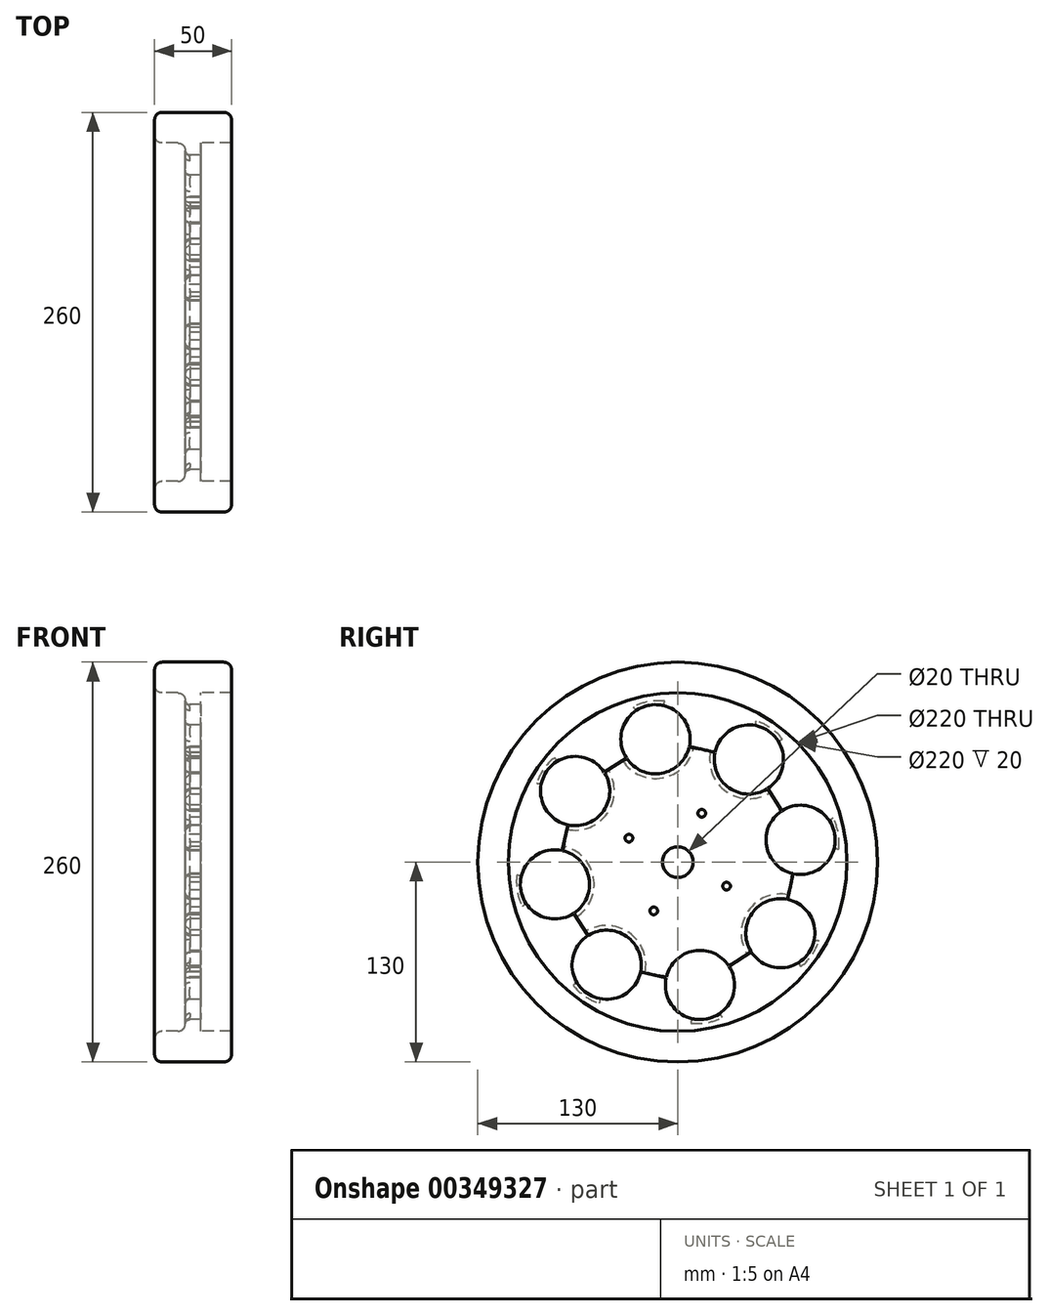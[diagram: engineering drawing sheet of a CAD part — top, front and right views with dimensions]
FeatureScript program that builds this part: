
annotation { "Feature Type Name" : "Feature", "Feature Type Description" : "" }
export const myFeature = defineFeature(function(context is Context, id is Id, definition is map)
    precondition{}
    {
        {
            var Q0;
            Q0=qCreatedBy(makeId("Right.planeOp"),FACE);
            var sketch = newSketch(context, id + "F0", { "sketchPlane" : qUnion([Q0])});
            skCircle(sketch, "E0", {"center": v(0, 0) * mm, "radius": 130 * mm});
            skCircle(sketch, "E1", {"center": v(0, 0) * mm, "radius": 110 * mm});
            skCircle(sketch, "E2", {"center": v(0, 0) * mm, "radius": 75 * mm});
            skCircle(sketch, "E3", {"center": v(0, 0) * mm, "radius": 10 * mm});
            skLineSegment(sketch, "E4.0", {"start": v(-31.73, 15.6) * mm, "end": v(15.6, 31.73) * mm});
            skLineSegment(sketch, "E4.1", {"start": v(15.6, 31.73) * mm, "end": v(31.73, -15.6) * mm});
            skLineSegment(sketch, "E4.2", {"start": v(31.73, -15.6) * mm, "end": v(-15.6, -31.73) * mm});
            skLineSegment(sketch, "E4.3", {"start": v(-15.6, -31.73) * mm, "end": v(-31.73, 15.6) * mm});
            skPoint(sketch, "E4.0.midPoint", {"position": v(-8.06, 23.66) * mm});
            skLineSegment(sketch, "E5.0", {"start": v(-66.72, 46.24) * mm, "end": v(-14.48, 79.88) * mm});
            skLineSegment(sketch, "E5.1", {"start": v(-14.48, 79.88) * mm, "end": v(46.24, 66.72) * mm});
            skLineSegment(sketch, "E5.2", {"start": v(46.24, 66.72) * mm, "end": v(79.88, 14.48) * mm});
            skLineSegment(sketch, "E5.3", {"start": v(79.88, 14.48) * mm, "end": v(66.72, -46.24) * mm});
            skLineSegment(sketch, "E5.4", {"start": v(66.72, -46.24) * mm, "end": v(14.48, -79.88) * mm});
            skLineSegment(sketch, "E5.5", {"start": v(14.48, -79.88) * mm, "end": v(-46.24, -66.72) * mm});
            skLineSegment(sketch, "E5.6", {"start": v(-46.24, -66.72) * mm, "end": v(-79.88, -14.48) * mm});
            skLineSegment(sketch, "E5.7", {"start": v(-79.88, -14.48) * mm, "end": v(-66.72, 46.24) * mm});
            skPoint(sketch, "E5.0.midPoint", {"position": v(-40.6, 63.06) * mm});
            skCircle(sketch, "E6", {"center": v(-31.73, 15.6) * mm, "radius": 2.5 * mm});
            skCircle(sketch, "E7", {"center": v(15.6, 31.73) * mm, "radius": 2.5 * mm});
            skCircle(sketch, "E8", {"center": v(31.73, -15.6) * mm, "radius": 2.5 * mm});
            skCircle(sketch, "E9", {"center": v(-15.6, -31.73) * mm, "radius": 2.5 * mm});
            skCircle(sketch, "E10", {"center": v(-46.24, -66.72) * mm, "radius": 22.5 * mm});
            skCircle(sketch, "E11", {"center": v(14.48, -79.88) * mm, "radius": 22.5 * mm});
            skCircle(sketch, "E12", {"center": v(66.72, -46.24) * mm, "radius": 22.5 * mm});
            skCircle(sketch, "E13", {"center": v(79.88, 14.48) * mm, "radius": 22.5 * mm});
            skCircle(sketch, "E14", {"center": v(46.24, 66.72) * mm, "radius": 22.5 * mm});
            skCircle(sketch, "E15", {"center": v(-14.48, 79.88) * mm, "radius": 22.5 * mm});
            skCircle(sketch, "E16", {"center": v(-66.72, 46.24) * mm, "radius": 22.5 * mm});
            skCircle(sketch, "E17", {"center": v(-79.88, -14.48) * mm, "radius": 22.5 * mm});
            skSolve(sketch);
        }
        {
            var Q0;
            Q0 = qSketchRegion(id + "F0", true);
            extrude(context, id + "F1", {"entities" : qUnion([Q0]), "endBound" : BoundingType.SYMMETRIC, "depth" : 50 * mm});
        }
        {
            var Q0;
            {var subQ0=sQuery(id+"F0.wireOp",EDGE,"E2");var subQ29=makeQuery(id+"F0.imprint","INTERSECT",VERTEX,{"derivedFrom":[subQ0,sQuery(id+"F0.wireOp",EDGE,"E5.2")]});Q0=makeQuery(id+"F0.imprint","IMPRINT",FACE,{"disambiguationData":[TD([[makeQuery(id+"F0.imprint","IMPRINT",EDGE,{"disambiguationData":[TD([[subQ29,1.0]])],"derivedFrom":subQ0}),1.0]])]});}
            var Q1;
            Q1=makeQuery(id+"F0.imprint","IMPRINT",FACE,{"disambiguationData":[TD([[makeQuery(id+"F0.imprint","IMPRINT",EDGE,{"derivedFrom":sQuery(id+"F0.wireOp",EDGE,"E1")}),1.0]])]});
            var Q2;
            Q2=makeQuery(id+"F0.imprint","IMPRINT",FACE,{"disambiguationData":[TD([[makeQuery(id+"F0.imprint","IMPRINT",EDGE,{"derivedFrom":sQuery(id+"F0.wireOp",EDGE,"E3")}),-1.0]])]});
            extrude(context, id + "F2", {"entities" : qUnion([Q0, Q1, Q2]), "operationType" : NewBodyOperationType.ADD, "endBound" : BoundingType.SYMMETRIC, "depth" : 10 * mm});
        }
        {
            var Q0;
            {var subQ0=sQuery(id+"F0.wireOp",EDGE,"E1");Q0=makeQuery(id+"F2.boolean.opBoolean","SPLIT",FACE,{"disambiguationData":[TD([makeQuery(id+"F1.opExtrude","CAP_FACE",FACE,{"disambiguationData":[OSD([sQuery(id+"F0.wireOp",EDGE,"E0"),subQ0])],"isStart":true})])],"derivedFrom":makeQuery(id+"F1.opExtrude","SWEPT_FACE",FACE,{"disambiguationData":[OSD([subQ0])]})});}
            fillet(context, id + "F3", {"entities" : qUnion([Q0]), "radius" : 5 * mm, "tangentPropagation" : true, "allowEdgeOverflow" : false});
        }
        {
            var Q0;
            Q0=makeQuery(id+"F1.opExtrude","CAP_EDGE",EDGE,{"disambiguationData":[OSD([sQuery(id+"F0.wireOp",EDGE,"E0")])],"isStart":true});
            var Q1;
            Q1=makeQuery(id+"F1.opExtrude","CAP_EDGE",EDGE,{"disambiguationData":[OSD([sQuery(id+"F0.wireOp",EDGE,"E0")])],"isStart":false});
            fillet(context, id + "F4", {"entities" : qUnion([Q0, Q1]), "radius" : 5 * mm, "tangentPropagation" : true, "allowEdgeOverflow" : false});
        }
        {
            var Q0;
            {var subQ0=sQuery(id+"F0.wireOp",EDGE,"E14");Q0=makeQuery(id+"F2.opExtrude","CAP_EDGE",EDGE,{"disambiguationData":[OSD([subQ0]),TDD([makeQuery(id+"F0.imprint","IMPRINT",EDGE,{"disambiguationData":[TD([[makeQuery(id+"F0.imprint","INTERSECT",VERTEX,{"derivedFrom":[sQuery(id+"F0.wireOp",EDGE,"E5.1"),subQ0]}),1.0]])],"derivedFrom":subQ0})])],"isStart":true});}
            var Q1;
            {var subQ0=sQuery(id+"F0.wireOp",EDGE,"E15");Q1=makeQuery(id+"F2.opExtrude","CAP_EDGE",EDGE,{"disambiguationData":[OSD([subQ0]),TDD([makeQuery(id+"F0.imprint","IMPRINT",EDGE,{"disambiguationData":[TD([[makeQuery(id+"F0.imprint","INTERSECT",VERTEX,{"derivedFrom":[sQuery(id+"F0.wireOp",EDGE,"E5.0"),subQ0]}),1.0]])],"derivedFrom":subQ0})])],"isStart":true});}
            var Q2;
            {var subQ0=sQuery(id+"F0.wireOp",EDGE,"E16");Q2=makeQuery(id+"F2.opExtrude","CAP_EDGE",EDGE,{"disambiguationData":[OSD([subQ0]),TDD([makeQuery(id+"F0.imprint","IMPRINT",EDGE,{"disambiguationData":[TD([[makeQuery(id+"F0.imprint","INTERSECT",VERTEX,{"derivedFrom":[sQuery(id+"F0.wireOp",EDGE,"E5.0"),subQ0]}),-1.0]])],"derivedFrom":subQ0})])],"isStart":true});}
            var Q3;
            {var subQ0=sQuery(id+"F0.wireOp",EDGE,"E13");Q3=makeQuery(id+"F2.opExtrude","CAP_EDGE",EDGE,{"disambiguationData":[OSD([subQ0]),TDD([makeQuery(id+"F0.imprint","IMPRINT",EDGE,{"disambiguationData":[TD([[makeQuery(id+"F0.imprint","INTERSECT",VERTEX,{"derivedFrom":[sQuery(id+"F0.wireOp",EDGE,"E5.2"),subQ0]}),1.0]])],"derivedFrom":subQ0})])],"isStart":true});}
            var Q4;
            {var subQ0=sQuery(id+"F0.wireOp",EDGE,"E12");Q4=makeQuery(id+"F2.opExtrude","CAP_EDGE",EDGE,{"disambiguationData":[OSD([subQ0]),TDD([makeQuery(id+"F0.imprint","IMPRINT",EDGE,{"disambiguationData":[TD([[makeQuery(id+"F0.imprint","INTERSECT",VERTEX,{"derivedFrom":[sQuery(id+"F0.wireOp",EDGE,"E5.3"),subQ0]}),1.0]])],"derivedFrom":subQ0})])],"isStart":true});}
            var Q5;
            {var subQ0=sQuery(id+"F0.wireOp",EDGE,"E11");Q5=makeQuery(id+"F2.opExtrude","CAP_EDGE",EDGE,{"disambiguationData":[OSD([subQ0]),TDD([makeQuery(id+"F0.imprint","IMPRINT",EDGE,{"disambiguationData":[TD([[makeQuery(id+"F0.imprint","INTERSECT",VERTEX,{"derivedFrom":[sQuery(id+"F0.wireOp",EDGE,"E5.4"),subQ0]}),1.0]])],"derivedFrom":subQ0})])],"isStart":true});}
            var Q6;
            {var subQ0=sQuery(id+"F0.wireOp",EDGE,"E17");Q6=makeQuery(id+"F2.opExtrude","CAP_EDGE",EDGE,{"disambiguationData":[OSD([subQ0]),TDD([makeQuery(id+"F0.imprint","IMPRINT",EDGE,{"disambiguationData":[TD([[makeQuery(id+"F0.imprint","INTERSECT",VERTEX,{"derivedFrom":[sQuery(id+"F0.wireOp",EDGE,"E5.6"),subQ0]}),1.0]])],"derivedFrom":subQ0})])],"isStart":true});}
            var Q7;
            {var subQ0=sQuery(id+"F0.wireOp",EDGE,"E10");Q7=makeQuery(id+"F2.opExtrude","CAP_EDGE",EDGE,{"disambiguationData":[OSD([subQ0]),TDD([makeQuery(id+"F0.imprint","IMPRINT",EDGE,{"disambiguationData":[TD([[makeQuery(id+"F0.imprint","INTERSECT",VERTEX,{"derivedFrom":[sQuery(id+"F0.wireOp",EDGE,"E5.5"),subQ0]}),1.0]])],"derivedFrom":subQ0})])],"isStart":true});}
            fillet(context, id + "F5", {"entities" : qUnion([Q0, Q1, Q2, Q3, Q4, Q5, Q6, Q7]), "radius" : 3 * mm, "tangentPropagation" : true, "allowEdgeOverflow" : false});
        }
        {
            var Q0;
            {var subQ0=sQuery(id+"F0.wireOp",EDGE,"E11");var subQ1=sQuery(id+"F0.wireOp",EDGE,"E2");Q0=makeQuery(id+"F2.opExtrude","CAP_EDGE",EDGE,{"disambiguationData":[OSD([subQ0]),TDD([makeQuery(id+"F0.imprint","IMPRINT",EDGE,{"disambiguationData":[TD([[makeQuery(id+"F0.imprint","INTERSECT",VERTEX,{"disambiguationData":[OD(0.0)],"derivedFrom":[subQ1,subQ0]}),1.0]])],"derivedFrom":subQ0})])],"isStart":true});}
            var Q1;
            {var subQ0=sQuery(id+"F0.wireOp",EDGE,"E10");var subQ1=sQuery(id+"F0.wireOp",EDGE,"E2");Q1=makeQuery(id+"F2.opExtrude","CAP_EDGE",EDGE,{"disambiguationData":[OSD([subQ0]),TDD([makeQuery(id+"F0.imprint","IMPRINT",EDGE,{"disambiguationData":[TD([[makeQuery(id+"F0.imprint","INTERSECT",VERTEX,{"disambiguationData":[OD(0.0)],"derivedFrom":[subQ1,subQ0]}),1.0]])],"derivedFrom":subQ0})])],"isStart":true});}
            var Q2;
            {var subQ0=sQuery(id+"F0.wireOp",EDGE,"E17");var subQ1=sQuery(id+"F0.wireOp",EDGE,"E2");Q2=makeQuery(id+"F2.opExtrude","CAP_EDGE",EDGE,{"disambiguationData":[OSD([subQ0]),TDD([makeQuery(id+"F0.imprint","IMPRINT",EDGE,{"disambiguationData":[TD([[makeQuery(id+"F0.imprint","INTERSECT",VERTEX,{"disambiguationData":[OD(0.0)],"derivedFrom":[subQ1,subQ0]}),1.0]])],"derivedFrom":subQ0})])],"isStart":true});}
            var Q3;
            {var subQ0=sQuery(id+"F0.wireOp",EDGE,"E16");var subQ1=sQuery(id+"F0.wireOp",EDGE,"E2");Q3=makeQuery(id+"F2.opExtrude","CAP_EDGE",EDGE,{"disambiguationData":[OSD([subQ0]),TDD([makeQuery(id+"F0.imprint","IMPRINT",EDGE,{"disambiguationData":[TD([[makeQuery(id+"F0.imprint","INTERSECT",VERTEX,{"disambiguationData":[OD(0.0)],"derivedFrom":[subQ1,subQ0]}),1.0]])],"derivedFrom":subQ0})])],"isStart":true});}
            var Q4;
            {var subQ0=sQuery(id+"F0.wireOp",EDGE,"E12");var subQ1=sQuery(id+"F0.wireOp",EDGE,"E2");Q4=makeQuery(id+"F2.opExtrude","CAP_EDGE",EDGE,{"disambiguationData":[OSD([subQ0]),TDD([makeQuery(id+"F0.imprint","IMPRINT",EDGE,{"disambiguationData":[TD([[makeQuery(id+"F0.imprint","INTERSECT",VERTEX,{"disambiguationData":[OD(0.0)],"derivedFrom":[subQ1,subQ0]}),1.0]])],"derivedFrom":subQ0})])],"isStart":true});}
            var Q5;
            {var subQ0=sQuery(id+"F0.wireOp",EDGE,"E13");var subQ1=sQuery(id+"F0.wireOp",EDGE,"E2");Q5=makeQuery(id+"F2.opExtrude","CAP_EDGE",EDGE,{"disambiguationData":[OSD([subQ0]),TDD([makeQuery(id+"F0.imprint","IMPRINT",EDGE,{"disambiguationData":[TD([[makeQuery(id+"F0.imprint","INTERSECT",VERTEX,{"disambiguationData":[OD(0.0)],"derivedFrom":[subQ1,subQ0]}),-1.0]])],"derivedFrom":subQ0})])],"isStart":true});}
            var Q6;
            {var subQ0=sQuery(id+"F0.wireOp",EDGE,"E14");var subQ1=sQuery(id+"F0.wireOp",EDGE,"E2");Q6=makeQuery(id+"F2.opExtrude","CAP_EDGE",EDGE,{"disambiguationData":[OSD([subQ0]),TDD([makeQuery(id+"F0.imprint","IMPRINT",EDGE,{"disambiguationData":[TD([[makeQuery(id+"F0.imprint","INTERSECT",VERTEX,{"disambiguationData":[OD(0.0)],"derivedFrom":[subQ1,subQ0]}),1.0]])],"derivedFrom":subQ0})])],"isStart":true});}
            var Q7;
            {var subQ0=sQuery(id+"F0.wireOp",EDGE,"E15");var subQ1=sQuery(id+"F0.wireOp",EDGE,"E2");Q7=makeQuery(id+"F2.opExtrude","CAP_EDGE",EDGE,{"disambiguationData":[OSD([subQ0]),TDD([makeQuery(id+"F0.imprint","IMPRINT",EDGE,{"disambiguationData":[TD([[makeQuery(id+"F0.imprint","INTERSECT",VERTEX,{"disambiguationData":[OD(0.0)],"derivedFrom":[subQ1,subQ0]}),1.0]])],"derivedFrom":subQ0})])],"isStart":true});}
            chamfer(context, id + "F6", {"entities" : qUnion([Q0, Q1, Q2, Q3, Q4, Q5, Q6, Q7]), "width" : 3 * mm, "tangentPropagation" : true});
        }
    });
